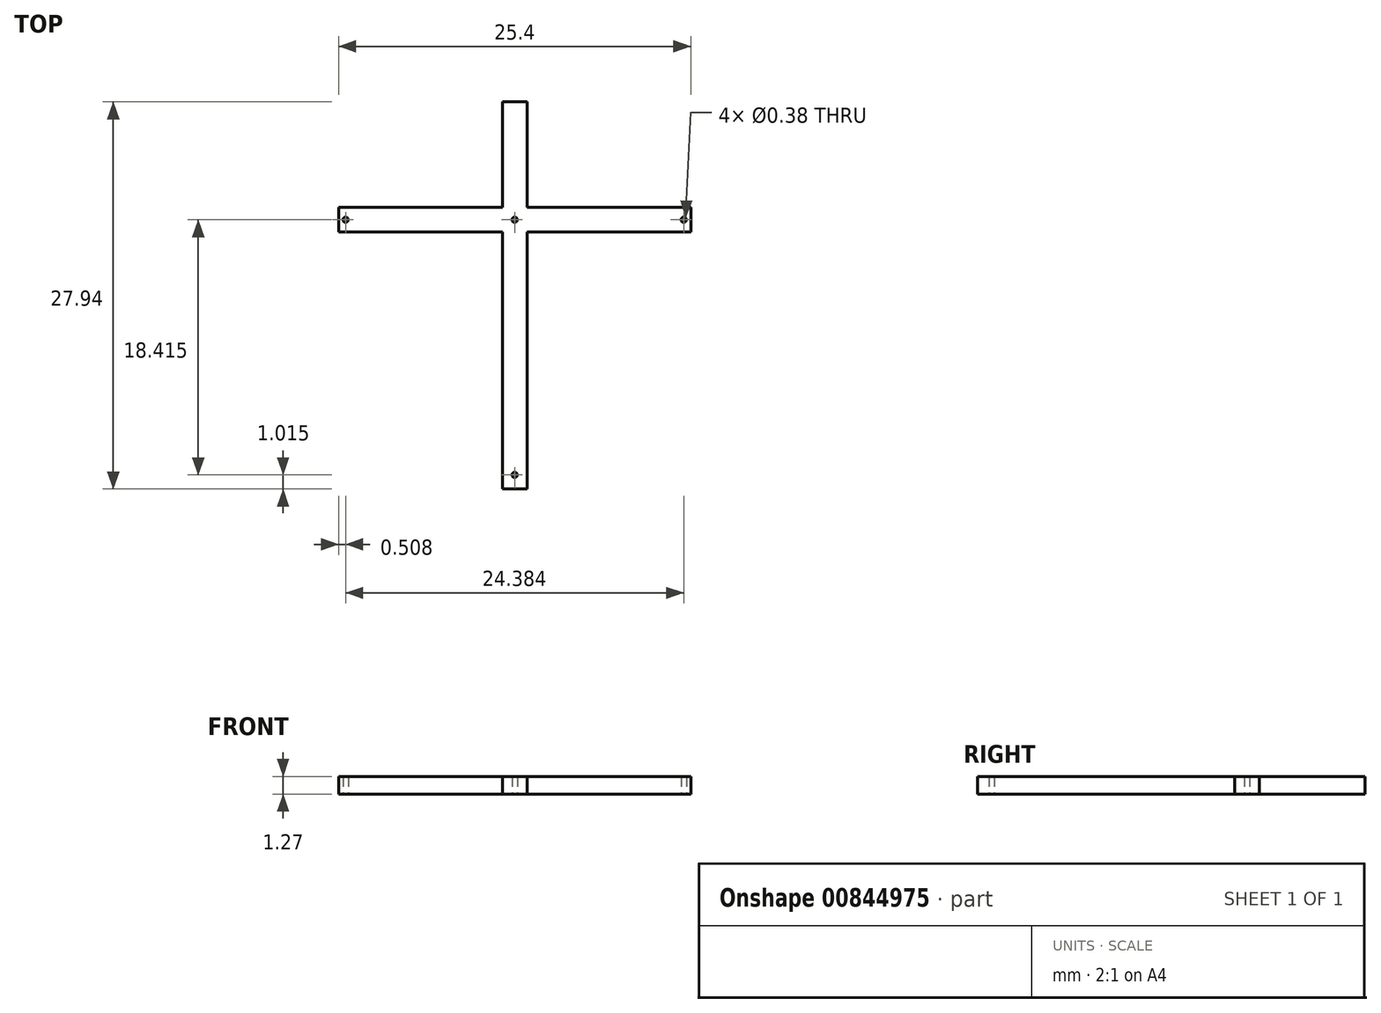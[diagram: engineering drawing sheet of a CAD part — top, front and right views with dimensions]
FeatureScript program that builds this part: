
annotation { "Feature Type Name" : "Feature", "Feature Type Description" : "" }
export const myFeature = defineFeature(function(context is Context, id is Id, definition is map)
    precondition{}
    {
        {
            var Q0;
            Q0=qCreatedBy(makeId("Top.planeOp"),FACE);
            var sketch = newSketch(context, id + "F0", { "sketchPlane" : qUnion([Q0])});
            skLineSegment(sketch, "E0.bottom", {"start": v(-12.7, 0.89) * mm, "end": v(-0.89, 0.89) * mm});
            skLineSegment(sketch, "E0.top", {"start": v(-12.7, -0.89) * mm, "end": v(-0.89, -0.89) * mm});
            skLineSegment(sketch, "E0.left", {"start": v(-12.7, 0.89) * mm, "end": v(-12.7, -0.89) * mm});
            skLineSegment(sketch, "E0.right", {"start": v(12.7, 0.89) * mm, "end": v(12.7, -0.89) * mm});
            skPoint(sketch, "E0.middle", {"position": v(0, 0) * mm});
            skCircle(sketch, "E1", {"center": v(12.2, 0) * mm, "radius": 0.2 * mm});
            skCircle(sketch, "E2", {"center": v(-12.2, 0) * mm, "radius": 0.2 * mm});
            skLineSegment(sketch, "E3.bottom", {"start": v(-0.89, 8.5) * mm, "end": v(0.89, 8.5) * mm});
            skLineSegment(sketch, "E3.top", {"start": v(-0.89, -19.43) * mm, "end": v(0.89, -19.43) * mm});
            skLineSegment(sketch, "E3.left", {"start": v(-0.89, 8.5) * mm, "end": v(-0.89, 0.89) * mm});
            skLineSegment(sketch, "E3.right", {"start": v(0.89, 8.5) * mm, "end": v(0.89, 0.89) * mm});
            skLineSegment(sketch, "E4.trimOffspring", {"start": v(0.89, 0.89) * mm, "end": v(12.7, 0.89) * mm});
            skLineSegment(sketch, "E5.trimOffspring", {"start": v(0.89, -0.89) * mm, "end": v(0.89, -19.43) * mm});
            skLineSegment(sketch, "E6.trimOffspring", {"start": v(0.89, -0.89) * mm, "end": v(12.7, -0.89) * mm});
            skLineSegment(sketch, "E7.trimOffspring", {"start": v(-0.89, -0.89) * mm, "end": v(-0.89, -19.43) * mm});
            skCircle(sketch, "E8", {"center": v(0, -18.41) * mm, "radius": 0.2 * mm});
            skCircle(sketch, "E9", {"center": v(0, 0) * mm, "radius": 0.2 * mm});
            skSolve(sketch);
        }
        {
            var Q0;
            Q0=qSketchRegion(id+"F0",true);
            extrude(context, id + "F1", {"entities" : qUnion([Q0]), "depth" : 1.27 * mm, "offsetDistance" : 25.4 * mm});
        }
    });
